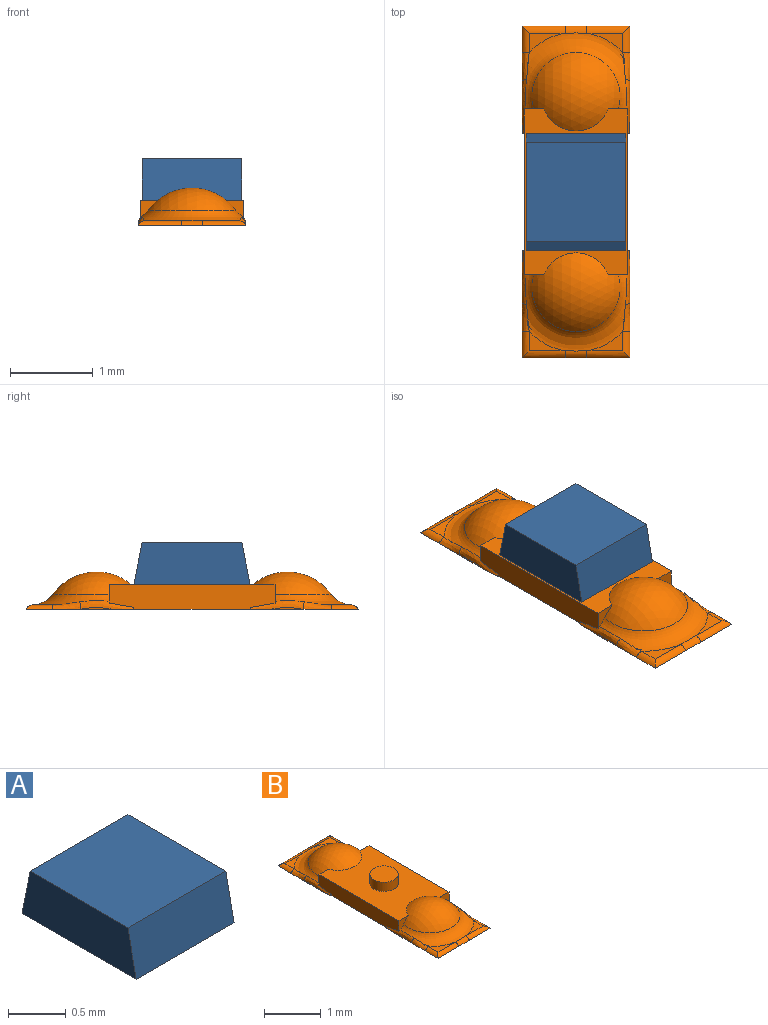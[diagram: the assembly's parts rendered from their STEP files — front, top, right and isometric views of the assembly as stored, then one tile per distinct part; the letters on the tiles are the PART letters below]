
ASSEMBLY  parts=2 mates=1
PART A: 6 faces, bbox 1.2x1.4x0.5 mm
  f0: plane 1.2x0.5mm, normal (0,0.98,0.2), area 0.6mm2, adj f1,f3,f4,f5
  f1: plane 1.4x1.2mm, normal (0,0,-1), area 1.7mm2, adj f0,f2,f4,f5
  f2: plane 1.2x0.5mm, normal (0,-0.98,0.2), area 0.6mm2, adj f1,f3,f4,f5
  f3: plane 1.2x1.2mm, normal (0,0,1), area 1.4mm2, adj f0,f2,f4,f5
  f4: plane 1.4x0.5mm, normal (-1,0,0), area 0.7mm2, adj f0,f1,f2,f3
  f5: plane 1.4x0.5mm, normal (1,0,0), area 0.7mm2, adj f0,f1,f2,f3
PART B: 44 faces, bbox 2.2x4.5x0.6 mm
  f0: torus R=0.77mm, axis (0,0,1), area 0.5mm2, adj f1,f5,f6,f14,f15,f35,f36,f39
  f1: sphere r=0.65mm, area 0.9mm2, adj f0,f11,f14,f15
  f2: torus R=0.77mm, axis (0,0,1), area 0.5mm2, adj f3,f7,f8,f12,f13,f22,f23,f26
  f3: sphere r=0.65mm, area 0.9mm2, adj f2,f11,f12,f13
  f4: cylinder r=0.25mm len=0.5mm, axis (0,0,1), area 0.3mm2, adj f11,f17
  f5: plane 0.43x0.23mm, normal (0,0,1), area 0mm2, adj f0,f37,f38
  f6: plane 0.43x0.23mm, normal (0,0,1), area 0mm2, adj f0,f40,f41
  f7: plane 0.43x0.23mm, normal (0,0,1), area 0mm2, adj f2,f24,f25
  f8: plane 0.43x0.23mm, normal (0,0,1), area 0mm2, adj f2,f27,f28
  f9: plane 2.02x0.32mm, normal (-1,0,0), area 0.6mm2, adj f11,f13,f14,f16,f18,f22,f31,f35
  f10: plane 2.02x0.32mm, normal (1,0,0), area 0.6mm2, adj f11,f12,f15,f16,f19,f30,f32,f43
  f11: plane 2x1.25mm, normal (0,0,1), area 2mm2, adj f1,f3,f4,f9,f10,f12,f13,f14
  f12: plane 0.25x0.24mm, normal (0,1,0), area 0mm2, adj f2,f3,f10,f11,f30
  f13: plane 0.25x0.24mm, normal (0,1,0), area 0mm2, adj f2,f3,f9,f11,f22
  f14: plane 0.25x0.24mm, normal (0,-1,0), area 0mm2, adj f0,f1,f9,f11,f35
  f15: plane 0.25x0.24mm, normal (0,-1,0), area 0mm2, adj f0,f1,f10,f11,f43
  f16: plane 4.01x1.31mm, normal (0,0,-1), area 5.1mm2, adj f9,f10,f18,f19,f20,f21,f22,f23
  f17: plane 0.5x0.5mm, normal (0,0,1), area 0.2mm2, adj f4
  f18: plane 0.02x0.02mm, normal (0,-1,0), area 0mm2, adj f9,f16,f22
  f19: plane 0.03x0.02mm, normal (0,-1,0), area 0mm2, adj f10,f16,f30
  f20: plane 0.38x0.02mm, normal (-1,0,0), area 0mm2, adj f16,f22
  f21: plane 0.38x0.02mm, normal (1,0,0), area 0mm2, adj f16,f30
  f22: bspline ~0.66x0.15mm, area 0.1mm2, adj f2,f9,f13,f16,f18,f20,f23
  f23: bspline ~0.34x0.09mm, area 0mm2, adj f2,f16,f22,f24
  f24: cylinder r=0.1mm len=0.32mm, axis (0,-1,0), area 0mm2, adj f7,f16,f23,f25
  f25: cylinder r=0.1mm len=0.52mm, axis (-1,0,0), area 0mm2, adj f7,f16,f24,f26
  f26: cylinder r=0.1mm len=0.26mm, axis (-1,0,0), area 0mm2, adj f2,f16,f25,f27
  f27: cylinder r=0.1mm len=0.52mm, axis (-1,0,0), area 0mm2, adj f8,f16,f26,f28
  f28: cylinder r=0.1mm len=0.32mm, axis (0,1,0), area 0mm2, adj f8,f16,f27,f29
  f29: bspline ~0.34x0.09mm, area 0mm2, adj f2,f16,f28,f30
  f30: bspline ~0.66x0.15mm, area 0.1mm2, adj f2,f10,f12,f16,f19,f21,f29
  f31: plane 0.03x0.02mm, normal (0,1,0), area 0mm2, adj f9,f16,f35
  f32: plane 0.02x0.02mm, normal (0,1,0), area 0mm2, adj f10,f16,f43
  f33: plane 0.38x0.02mm, normal (1,0,0), area 0mm2, adj f16,f43
  f34: plane 0.38x0.02mm, normal (-1,0,0), area 0mm2, adj f16,f35
  f35: bspline ~0.66x0.15mm, area 0.1mm2, adj f0,f9,f14,f16,f31,f34,f36
  f36: bspline ~0.34x0.09mm, area 0mm2, adj f0,f16,f35,f37
  f37: cylinder r=0.1mm len=0.32mm, axis (0,1,0), area 0mm2, adj f5,f16,f36,f38
  f38: cylinder r=0.1mm len=0.52mm, axis (-1,0,0), area 0mm2, adj f5,f16,f37,f39
  f39: cylinder r=0.1mm len=0.26mm, axis (-1,0,0), area 0mm2, adj f0,f16,f38,f40
  f40: cylinder r=0.1mm len=0.52mm, axis (-1,0,0), area 0mm2, adj f6,f16,f39,f41
  f41: cylinder r=0.1mm len=0.32mm, axis (0,-1,0), area 0mm2, adj f6,f16,f40,f42
  f42: bspline ~0.34x0.09mm, area 0mm2, adj f0,f16,f41,f43
  f43: bspline ~0.66x0.15mm, area 0.1mm2, adj f0,f10,f15,f16,f32,f33,f42
PLACE A t=(17.66,-25.88,12.22)mm
PLACE B t=(17.66,-25.88,12.22)mm
MATE fastened A.f1 <-> B.f4  axis (0,0,-1) through (-18.91,32.54,12.52)mm
